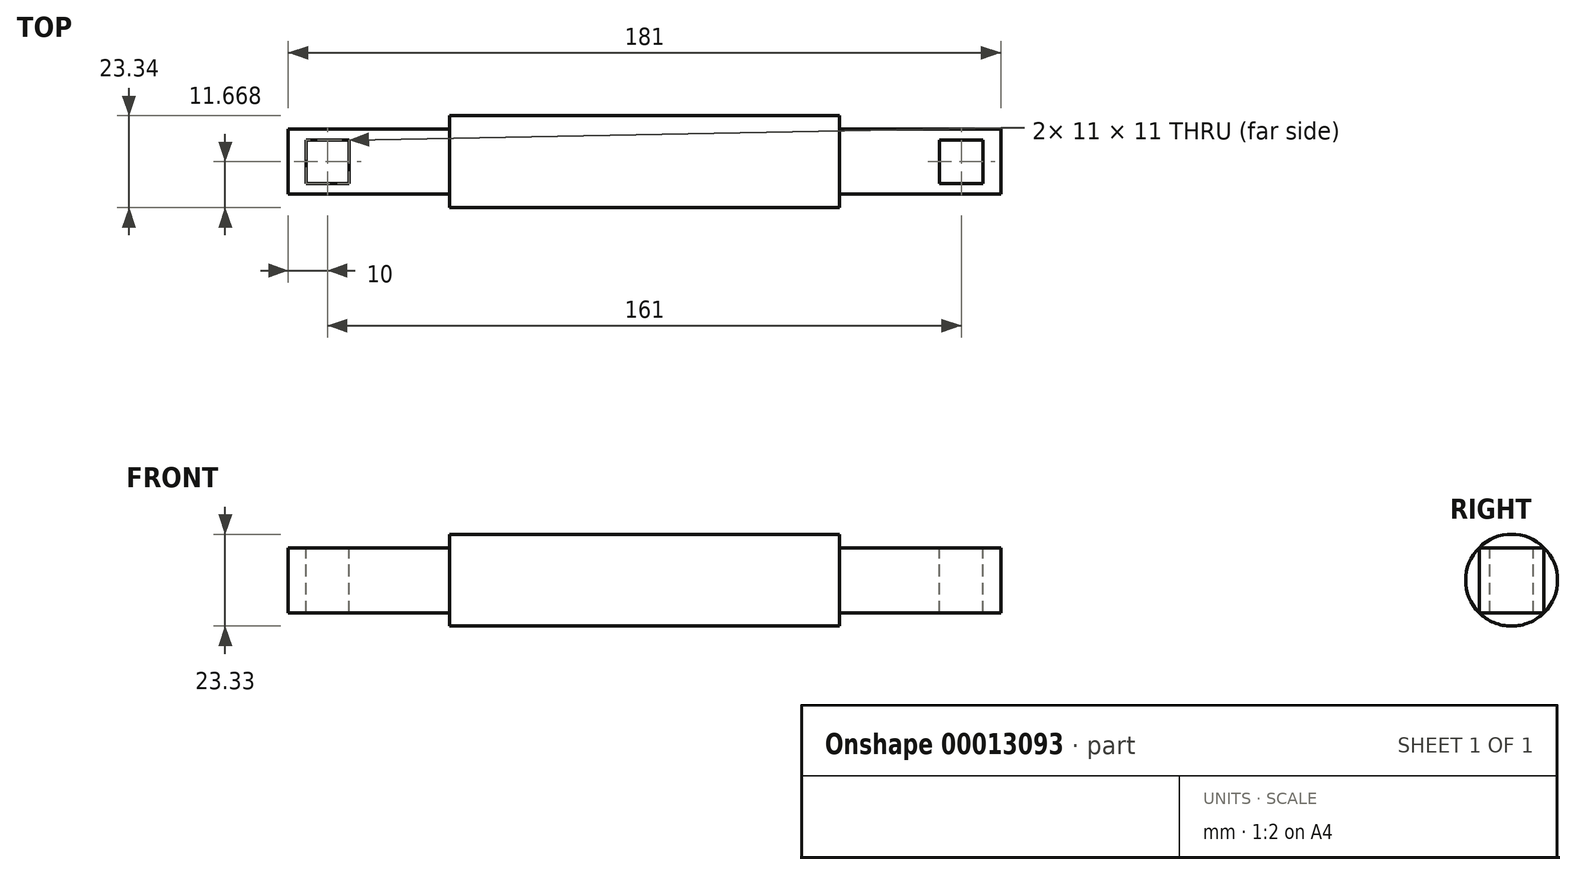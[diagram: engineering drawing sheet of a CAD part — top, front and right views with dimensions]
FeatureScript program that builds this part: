
annotation { "Feature Type Name" : "Feature", "Feature Type Description" : "" }
export const myFeature = defineFeature(function(context is Context, id is Id, definition is map)
    precondition{}
    {
        {
            var Q0;
            Q0=qCreatedBy(makeId("Right.planeOp"),FACE);
            var sketch = newSketch(context, id + "F0", { "sketchPlane" : qUnion([Q0])});
            skCircle(sketch, "E0", {"center": v(-39.44, 24.64) * mm, "radius": 11.67 * mm});
            skLineSegment(sketch, "E1.rect.bottom", {"start": v(-47.7, 16.4) * mm, "end": v(-31.2, 16.4) * mm, "construction": true});
            skLineSegment(sketch, "E1.rect.top", {"start": v(-47.7, 32.9) * mm, "end": v(-31.2, 32.9) * mm, "construction": true});
            skLineSegment(sketch, "E1.rect.left", {"start": v(-47.7, 16.4) * mm, "end": v(-47.7, 32.9) * mm, "construction": true});
            skLineSegment(sketch, "E1.rect.right", {"start": v(-31.2, 16.4) * mm, "end": v(-31.2, 32.9) * mm, "construction": true});
            skSolve(sketch);
        }
        {
            var Q0;
            Q0=makeQuery(id+"F0.imprint","IMPRINT",FACE,{"disambiguationData":[TD([[makeQuery(id+"F0.imprint","IMPRINT",EDGE,{"derivedFrom":sQuery(id+"F0.wireOp",EDGE,"E0")}),1.0]])]});
            extrude(context, id + "F1", {"entities" : qUnion([Q0]), "depth" : 99 * mm});
        }
        {
            var Q0;
            Q0=makeQuery(id+"F1.opExtrude","CAP_FACE",FACE,{"disambiguationData":[OSD([sQuery(id+"F0.wireOp",EDGE,"E0")])],"isStart":false});
            var sketch = newSketch(context, id + "F2", { "sketchPlane" : qUnion([Q0])});
            skCircle(sketch, "E2.0", {"center": v(-39.44, 24.64) * mm, "radius": 11.67 * mm});
            skLineSegment(sketch, "E3.rect.bottom", {"start": v(-31.2, 16.4) * mm, "end": v(-47.7, 16.4) * mm});
            skLineSegment(sketch, "E3.rect.top", {"start": v(-31.2, 32.9) * mm, "end": v(-47.7, 32.9) * mm});
            skLineSegment(sketch, "E3.rect.left", {"start": v(-31.2, 16.4) * mm, "end": v(-31.2, 32.9) * mm});
            skLineSegment(sketch, "E3.rect.right", {"start": v(-47.7, 16.4) * mm, "end": v(-47.7, 32.9) * mm});
            skSolve(sketch);
        }
        {
            var Q0;
            Q0=makeQuery(id+"F2.imprint","IMPRINT",FACE,{"disambiguationData":[TD([[makeQuery(id+"F2.imprint","IMPRINT",EDGE,{"derivedFrom":sQuery(id+"F2.wireOp",EDGE,"E3.rect.bottom")}),-1.0]])]});
            extrude(context, id + "F3", {"entities" : qUnion([Q0]), "operationType" : NewBodyOperationType.ADD, "depth" : 41 * mm});
        }
        {
            var Q0;
            Q0=makeQuery(id+"F1.opExtrude","CAP_FACE",FACE,{"disambiguationData":[OSD([sQuery(id+"F0.wireOp",EDGE,"E0")])],"isStart":true});
            var sketch = newSketch(context, id + "F4", { "sketchPlane" : qUnion([Q0])});
            skCircle(sketch, "E4.0", {"center": v(39.44, 24.64) * mm, "radius": 11.67 * mm});
            skLineSegment(sketch, "E5.rect.bottom", {"start": v(47.7, 16.4) * mm, "end": v(31.2, 16.4) * mm});
            skLineSegment(sketch, "E5.rect.top", {"start": v(47.7, 32.9) * mm, "end": v(31.2, 32.9) * mm});
            skLineSegment(sketch, "E5.rect.left", {"start": v(47.7, 16.4) * mm, "end": v(47.7, 32.9) * mm});
            skLineSegment(sketch, "E5.rect.right", {"start": v(31.2, 16.4) * mm, "end": v(31.2, 32.9) * mm});
            skSolve(sketch);
        }
        {
            var Q0;
            Q0=makeQuery(id+"F4.imprint","IMPRINT",FACE,{"disambiguationData":[TD([[makeQuery(id+"F4.imprint","IMPRINT",EDGE,{"derivedFrom":sQuery(id+"F4.wireOp",EDGE,"E5.rect.bottom")}),-1.0]])]});
            extrude(context, id + "F5", {"entities" : qUnion([Q0]), "operationType" : NewBodyOperationType.ADD, "depth" : 41 * mm});
        }
        {
            var Q0;
            Q0=makeQuery(id+"F3.opExtrude","SWEPT_FACE",FACE,{"disambiguationData":[OSD([sQuery(id+"F2.wireOp",EDGE,"E3.rect.top")])]});
            var sketch = newSketch(context, id + "F6", { "sketchPlane" : qUnion([Q0])});
            skLineSegment(sketch, "E6.0", {"start": v(140, -31.2) * mm, "end": v(99, -31.2) * mm});
            skLineSegment(sketch, "E7.0", {"start": v(140, -31.2) * mm, "end": v(140, -47.7) * mm});
            skLineSegment(sketch, "E8.0", {"start": v(140, -47.7) * mm, "end": v(99, -47.7) * mm});
            skLineSegment(sketch, "E9.0.0", {"start": v(99, -31.2) * mm, "end": v(99, -47.7) * mm});
            skLineSegment(sketch, "E9.0.1", {"start": v(99, -47.7) * mm, "end": v(140, -47.7) * mm});
            skLineSegment(sketch, "E9.0.2", {"start": v(140, -47.7) * mm, "end": v(140, -31.2) * mm});
            skLineSegment(sketch, "E10", {"start": v(140, -39.44) * mm, "end": v(99, -39.44) * mm, "construction": true});
            skPoint(sketch, "E11", {"position": v(124.5, -39.44) * mm});
            skPoint(sketch, "E12", {"position": v(135.5, -39.44) * mm});
            skLineSegment(sketch, "E13", {"start": v(135.5, -39.44) * mm, "end": v(135.5, -33.94) * mm});
            skLineSegment(sketch, "E14", {"start": v(124.5, -39.44) * mm, "end": v(124.5, -33.94) * mm});
            skLineSegment(sketch, "E15", {"start": v(135.5, -33.94) * mm, "end": v(124.5, -33.94) * mm});
            skLineSegment(sketch, "E16.0.MirrorCS", {"start": v(124.5, -39.44) * mm, "end": v(124.5, -44.94) * mm});
            skLineSegment(sketch, "E17.0.MirrorCS", {"start": v(135.5, -44.94) * mm, "end": v(124.5, -44.94) * mm});
            skLineSegment(sketch, "E18.0.MirrorCS", {"start": v(135.5, -39.44) * mm, "end": v(135.5, -44.94) * mm});
            skSolve(sketch);
        }
        {
            var Q0;
            Q0=makeQuery(id+"F6.imprint","IMPRINT",FACE,{"disambiguationData":[TD([[makeQuery(id+"F6.imprint","IMPRINT",EDGE,{"derivedFrom":sQuery(id+"F6.wireOp",EDGE,"E13")}),1.0]])]});
            extrude(context, id + "F7", {"entities" : qUnion([Q0]), "operationType" : NewBodyOperationType.REMOVE, "endBound" : BoundingType.UP_TO_NEXT, "oppositeDirection" : true, "depth" : 25 * mm});
        }
        {
            var Q0;
            Q0=makeQuery(id+"F5.opExtrude","SWEPT_FACE",FACE,{"disambiguationData":[OSD([sQuery(id+"F4.wireOp",EDGE,"E5.rect.top")])]});
            var sketch = newSketch(context, id + "F8", { "sketchPlane" : qUnion([Q0])});
            skLineSegment(sketch, "E19.0", {"start": v(-41, -47.7) * mm, "end": v(-41, -31.2) * mm});
            skLineSegment(sketch, "E20.0", {"start": v(-41, -31.2) * mm, "end": v(0, -31.2) * mm});
            skLineSegment(sketch, "E21.0", {"start": v(-41, -47.7) * mm, "end": v(0, -47.7) * mm});
            skLineSegment(sketch, "E22.0", {"start": v(0, -47.7) * mm, "end": v(0, -31.2) * mm});
            skLineSegment(sketch, "E23", {"start": v(-41, -39.44) * mm, "end": v(0, -39.44) * mm, "construction": true});
            skPoint(sketch, "E24", {"position": v(-36.5, -39.44) * mm});
            skPoint(sketch, "E25", {"position": v(-25.5, -39.44) * mm});
            skLineSegment(sketch, "E26", {"start": v(-36.5, -39.44) * mm, "end": v(-36.5, -33.94) * mm});
            skLineSegment(sketch, "E27", {"start": v(-25.5, -39.44) * mm, "end": v(-25.5, -33.94) * mm});
            skLineSegment(sketch, "E28", {"start": v(-36.5, -33.94) * mm, "end": v(-25.5, -33.94) * mm});
            skLineSegment(sketch, "E29.0.MirrorCS", {"start": v(-36.5, -39.44) * mm, "end": v(-36.5, -44.94) * mm});
            skLineSegment(sketch, "E30.0.MirrorCS", {"start": v(-36.5, -44.94) * mm, "end": v(-25.5, -44.94) * mm});
            skLineSegment(sketch, "E31.0.MirrorCS", {"start": v(-25.5, -39.44) * mm, "end": v(-25.5, -44.94) * mm});
            skSolve(sketch);
        }
        {
            var Q0;
            Q0=makeQuery(id+"F8.imprint","IMPRINT",FACE,{"disambiguationData":[TD([[makeQuery(id+"F8.imprint","IMPRINT",EDGE,{"derivedFrom":sQuery(id+"F8.wireOp",EDGE,"E26")}),-1.0]])]});
            extrude(context, id + "F9", {"entities" : qUnion([Q0]), "operationType" : NewBodyOperationType.REMOVE, "endBound" : BoundingType.UP_TO_NEXT, "oppositeDirection" : true, "depth" : 25 * mm});
        }
    });
